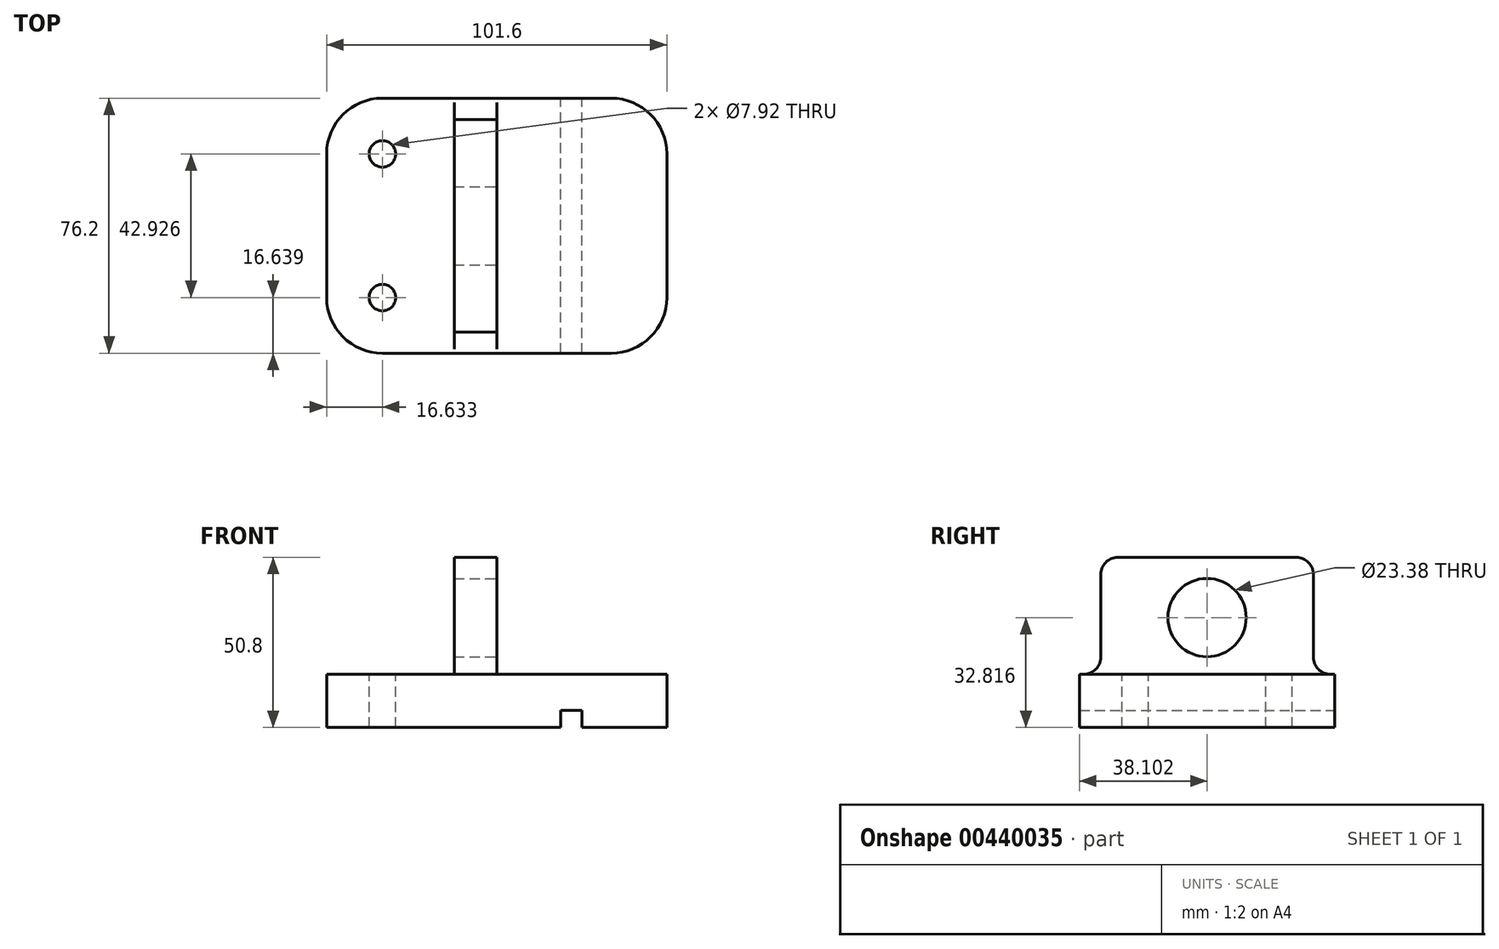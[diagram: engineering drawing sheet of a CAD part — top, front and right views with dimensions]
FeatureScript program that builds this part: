
annotation { "Feature Type Name" : "Feature", "Feature Type Description" : "" }
export const myFeature = defineFeature(function(context is Context, id is Id, definition is map)
    precondition{}
    {
        {
            var Q0;
            Q0=qCreatedBy(makeId("Top.planeOp"),FACE);
            var sketch = newSketch(context, id + "F0", { "sketchPlane" : qUnion([Q0])});
            skLineSegment(sketch, "E0.bottom", {"start": v(-49.42, 49.1) * mm, "end": v(52.18, 49.1) * mm});
            skLineSegment(sketch, "E0.top", {"start": v(-49.42, -27.1) * mm, "end": v(52.18, -27.1) * mm});
            skLineSegment(sketch, "E0.left", {"start": v(-49.42, 49.1) * mm, "end": v(-49.42, -27.1) * mm});
            skLineSegment(sketch, "E0.right", {"start": v(52.18, 49.1) * mm, "end": v(52.18, -27.1) * mm});
            skSolve(sketch);
        }
        {
            var Q0;
            Q0=makeQuery(id+"F0.imprint","IMPRINT",FACE,{"disambiguationData":[TD([[makeQuery(id+"F0.imprint","IMPRINT",EDGE,{"derivedFrom":sQuery(id+"F0.wireOp",EDGE,"E0.bottom")}),-1.0]])]});
            extrude(context, id + "F1", {"entities" : qUnion([Q0]), "depth" : 15.88 * mm});
        }
        {
            var Q0;
            Q0=makeQuery(id+"F1.opExtrude","CAP_FACE",FACE,{"disambiguationData":[OSD([sQuery(id+"F0.wireOp",EDGE,"E0.bottom"),sQuery(id+"F0.wireOp",EDGE,"E0.top"),sQuery(id+"F0.wireOp",EDGE,"E0.left"),sQuery(id+"F0.wireOp",EDGE,"E0.right")])],"isStart":false});
            var sketch = newSketch(context, id + "F2", { "sketchPlane" : qUnion([Q0])});
            skCircle(sketch, "E1", {"center": v(-32.79, 32.46) * mm, "radius": 3.96 * mm});
            skCircle(sketch, "E2", {"center": v(-32.79, -10.47) * mm, "radius": 3.96 * mm});
            skSolve(sketch);
        }
        {
            var Q0;
            Q0 = qSketchRegion(id + "F2", true);
            extrude(context, id + "F3", {"entities" : qUnion([Q0]), "operationType" : NewBodyOperationType.REMOVE, "oppositeDirection" : true, "depth" : 15.88 * mm});
        }
        {
            var Q0;
            Q0=makeQuery(id+"F1.opExtrude","SWEPT_EDGE",EDGE,{"disambiguationData":[OSD([sQuery(id+"F0.wireOp",EDGE,"E0.bottom"),sQuery(id+"F0.wireOp",EDGE,"E0.left")])]});
            var Q1;
            Q1=makeQuery(id+"F1.opExtrude","SWEPT_EDGE",EDGE,{"disambiguationData":[OSD([sQuery(id+"F0.wireOp",EDGE,"E0.bottom"),sQuery(id+"F0.wireOp",EDGE,"E0.right")])]});
            var Q2;
            Q2=makeQuery(id+"F1.opExtrude","SWEPT_EDGE",EDGE,{"disambiguationData":[OSD([sQuery(id+"F0.wireOp",EDGE,"E0.top"),sQuery(id+"F0.wireOp",EDGE,"E0.right")])]});
            var Q3;
            Q3=makeQuery(id+"F1.opExtrude","SWEPT_EDGE",EDGE,{"disambiguationData":[OSD([sQuery(id+"F0.wireOp",EDGE,"E0.top"),sQuery(id+"F0.wireOp",EDGE,"E0.left")])]});
            fillet(context, id + "F4", {"entities" : qUnion([Q0, Q1, Q2, Q3]), "radius" : 16.64 * mm, "tangentPropagation" : true, "allowEdgeOverflow" : false});
        }
        {
            var Q0;
            Q0=qCreatedBy(makeId("Top.planeOp"),FACE);
            var sketch = newSketch(context, id + "F5", { "sketchPlane" : qUnion([Q0])});
            skLineSegment(sketch, "E3.bottom", {"start": v(-11.32, 42.74) * mm, "end": v(1.38, 42.74) * mm});
            skLineSegment(sketch, "E3.top", {"start": v(-11.32, -20.76) * mm, "end": v(1.38, -20.76) * mm});
            skLineSegment(sketch, "E3.left", {"start": v(-11.32, 42.74) * mm, "end": v(-11.32, -20.76) * mm});
            skLineSegment(sketch, "E3.right", {"start": v(1.38, 42.74) * mm, "end": v(1.38, -20.76) * mm});
            skSolve(sketch);
        }
        {
            var Q0;
            Q0 = qSketchRegion(id + "F5", true);
            extrude(context, id + "F6", {"entities" : qUnion([Q0]), "operationType" : NewBodyOperationType.ADD, "depth" : 50.8 * mm});
        }
        {
            var Q0;
            Q0=makeQuery(id+"F6.opExtrude","CAP_EDGE",EDGE,{"disambiguationData":[OSD([sQuery(id+"F5.wireOp",EDGE,"E3.bottom")])],"isStart":false});
            var Q1;
            Q1=makeQuery(id+"F6.opExtrude","CAP_EDGE",EDGE,{"disambiguationData":[OSD([sQuery(id+"F5.wireOp",EDGE,"E3.top")])],"isStart":false});
            var Q2;
            Q2=makeQuery(id+"F6.boolean.opBoolean","INTERSECT",EDGE,{"derivedFrom":[makeQuery(id+"F1.opExtrude","CAP_FACE",FACE,{"disambiguationData":[OSD([sQuery(id+"F0.wireOp",EDGE,"E0.bottom"),sQuery(id+"F0.wireOp",EDGE,"E0.top"),sQuery(id+"F0.wireOp",EDGE,"E0.left"),sQuery(id+"F0.wireOp",EDGE,"E0.right")])],"isStart":false}),makeQuery(id+"F6.opExtrude","SWEPT_FACE",FACE,{"disambiguationData":[OSD([sQuery(id+"F5.wireOp",EDGE,"E3.top")])]})]});
            var Q3;
            Q3=makeQuery(id+"F6.boolean.opBoolean","INTERSECT",EDGE,{"derivedFrom":[makeQuery(id+"F1.opExtrude","CAP_FACE",FACE,{"disambiguationData":[OSD([sQuery(id+"F0.wireOp",EDGE,"E0.bottom"),sQuery(id+"F0.wireOp",EDGE,"E0.top"),sQuery(id+"F0.wireOp",EDGE,"E0.left"),sQuery(id+"F0.wireOp",EDGE,"E0.right")])],"isStart":false}),makeQuery(id+"F6.opExtrude","SWEPT_FACE",FACE,{"disambiguationData":[OSD([sQuery(id+"F5.wireOp",EDGE,"E3.bottom")])]})]});
            fillet(context, id + "F7", {"entities" : qUnion([Q0, Q1, Q2, Q3]), "radius" : 5.08 * mm, "tangentPropagation" : true, "allowEdgeOverflow" : false});
        }
        {
            var Q0;
            Q0=makeQuery(id+"F6.opExtrude","SWEPT_FACE",FACE,{"disambiguationData":[OSD([sQuery(id+"F5.wireOp",EDGE,"E3.right")])]});
            var sketch = newSketch(context, id + "F8", { "sketchPlane" : qUnion([Q0])});
            skCircle(sketch, "E4", {"center": v(11, 32.82) * mm, "radius": 11.69 * mm});
            skSolve(sketch);
        }
        {
            var Q0;
            Q0 = qSketchRegion(id + "F8", true);
            var Q1;
            Q1=sQuery(id+"F8.wireOp",EDGE,"E4");
            extrude(context, id + "F9", {"entities" : qUnion([Q0]), "operationType" : NewBodyOperationType.REMOVE, "surfaceEntities" : qUnion([Q1]), "oppositeDirection" : true, "depth" : 25.4 * mm});
        }
        {
            var Q0;
            Q0=makeQuery(id+"F1.opExtrude","SWEPT_FACE",FACE,{"disambiguationData":[OSD([sQuery(id+"F0.wireOp",EDGE,"E0.bottom")])]});
            var sketch = newSketch(context, id + "F10", { "sketchPlane" : qUnion([Q0])});
            skLineSegment(sketch, "E5", {"start": v(-26.78, 0) * mm, "end": v(-26.78, 5.08) * mm});
            skLineSegment(sketch, "E6", {"start": v(-26.78, 5.08) * mm, "end": v(-20.43, 5.08) * mm});
            skLineSegment(sketch, "E7", {"start": v(-20.43, 5.08) * mm, "end": v(-20.43, 0) * mm});
            skLineSegment(sketch, "E8", {"start": v(-20.43, 0) * mm, "end": v(-26.78, 0) * mm});
            skSolve(sketch);
        }
        {
            var Q0;
            Q0 = qSketchRegion(id + "F10", true);
            extrude(context, id + "F11", {"entities" : qUnion([Q0]), "operationType" : NewBodyOperationType.REMOVE, "oppositeDirection" : true, "depth" : 101.6 * mm});
        }
    });
